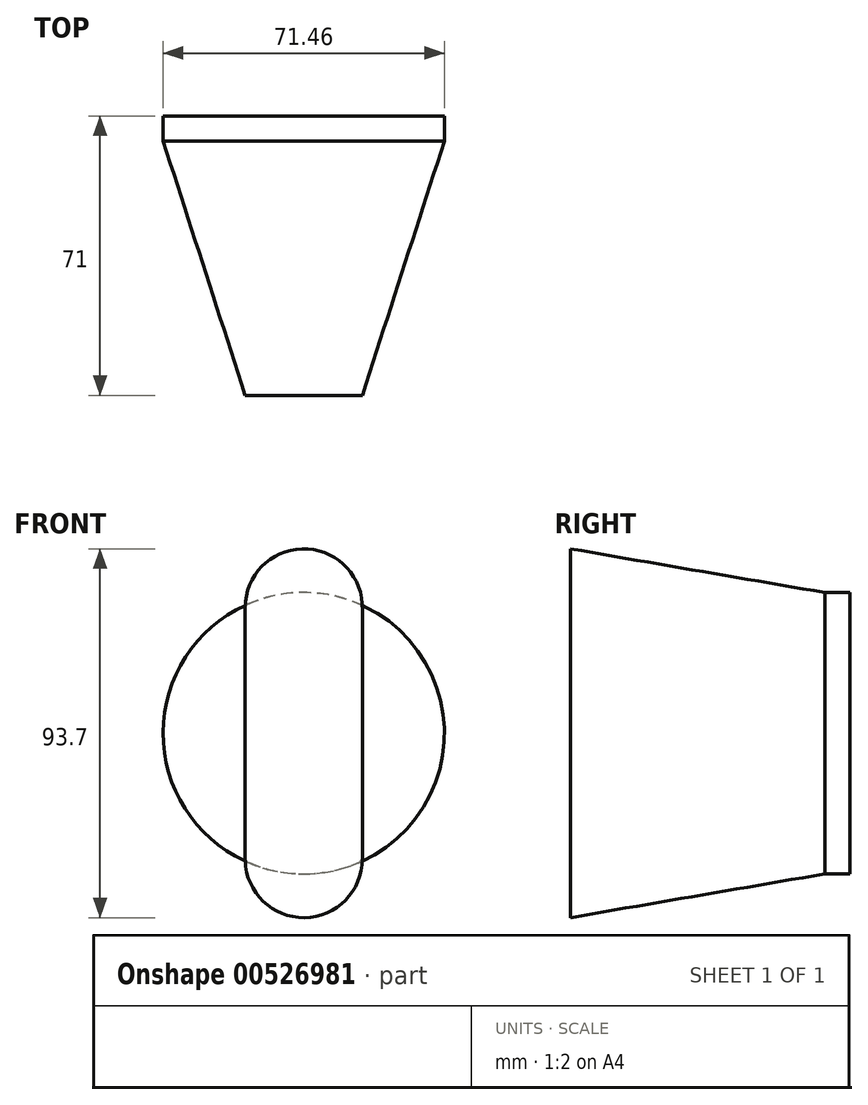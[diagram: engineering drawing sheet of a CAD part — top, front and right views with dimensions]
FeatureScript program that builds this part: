
annotation { "Feature Type Name" : "Feature", "Feature Type Description" : "" }
export const myFeature = defineFeature(function(context is Context, id is Id, definition is map)
    precondition{}
    {
        {
            var Q0;
            Q0=qCreatedBy(makeId("Front.planeOp"),FACE);
            var sketch = newSketch(context, id + "F0", { "sketchPlane" : qUnion([Q0])});
            skCircle(sketch, "E0", {"center": v(0, 0) * mm, "radius": 35.73 * mm});
            skSolve(sketch);
        }
        {
            var Q0;
            Q0=qCreatedBy(makeId("Front.planeOp"),FACE);
            cPlane(context, id + "F1", {"entities" : qUnion([Q0]), "cplaneType" : CPlaneType.OFFSET, "offset" : 67.82 * mm, "width" : 152.4 * mm, "height" : 152.4 * mm});
        }
        {
            var Q0;
            Q0=qCreatedBy(id+"F1.planeOp",FACE);
            var sketch = newSketch(context, id + "F2", { "sketchPlane" : qUnion([Q0])});
            skLineSegment(sketch, "E1.bottom", {"start": v(14.86, -32) * mm, "end": v(-14.86, -32) * mm, "construction": true});
            skLineSegment(sketch, "E1.top", {"start": v(14.86, 32) * mm, "end": v(-14.86, 32) * mm, "construction": true});
            skLineSegment(sketch, "E1.left", {"start": v(14.86, -32) * mm, "end": v(14.86, 32) * mm});
            skLineSegment(sketch, "E1.right", {"start": v(-14.86, -32) * mm, "end": v(-14.86, 32) * mm});
            skPoint(sketch, "E1.middle", {"position": v(0, 0) * mm});
            skArc(sketch, "E2", {"start": v(14.86, 32) * mm, "mid": v(0, 46.85) * mm, "end": v(-14.86, 32) * mm});
            skArc(sketch, "E3", {"start": v(-14.86, -32) * mm, "mid": v(0, -46.85) * mm, "end": v(14.86, -32) * mm});
            skSolve(sketch);
        }
        {
            var Q0;
            Q0=makeQuery(id+"F0.imprint","IMPRINT",FACE,{"disambiguationData":[TD([[makeQuery(id+"F0.imprint","IMPRINT",EDGE,{"derivedFrom":sQuery(id+"F0.wireOp",EDGE,"E0")}),1.0]])]});
            extrude(context, id + "F3", {"entities" : qUnion([Q0]), "endBound" : BoundingType.SYMMETRIC, "depth" : 6.35 * mm, "offsetDistance" : 25.4 * mm});
        }
        {
            var Q0;
            Q0=makeQuery(id+"F3.opExtrude","CAP_FACE",FACE,{"disambiguationData":[OSD([sQuery(id+"F0.wireOp",EDGE,"E0")])],"isStart":false});
            var sketch = newSketch(context, id + "F4", { "sketchPlane" : qUnion([Q0])});
            skArc(sketch, "E4", {"start": v(-14.65, 32.6) * mm, "mid": v(-35.73, 0.27) * mm, "end": v(-15.14, -32.37) * mm});
            skArc(sketch, "E5", {"start": v(15.62, 32.14) * mm, "mid": v(0.53, 35.73) * mm, "end": v(-14.65, 32.6) * mm});
            skArc(sketch, "E6", {"start": v(14.18, -32.8) * mm, "mid": v(35.72, -0.8) * mm, "end": v(15.62, 32.14) * mm});
            skArc(sketch, "E7", {"start": v(-15.14, -32.37) * mm, "mid": v(-0.53, -35.73) * mm, "end": v(14.18, -32.8) * mm});
            skSolve(sketch);
        }
        {
            var Q1;
            Q1=makeQuery(id+"F4.imprint","IMPRINT",FACE,{"disambiguationData":[TD([[makeQuery(id+"F4.imprint","IMPRINT",EDGE,{"derivedFrom":sQuery(id+"F4.wireOp",EDGE,"E4")}),1.0]])]});
            var Q2;
            Q2=makeQuery(id+"F2.imprint","IMPRINT",FACE,{"disambiguationData":[TD([[makeQuery(id+"F2.imprint","IMPRINT",EDGE,{"derivedFrom":sQuery(id+"F2.wireOp",EDGE,"E1.left")}),1.0]])]});
            loft(context, id + "F5", {"operationType" : NewBodyOperationType.ADD, "sheetProfilesArray" : [{ "sheetProfileEntities" : qUnion([Q1]) }, { "sheetProfileEntities" : qUnion([Q2]) }]});
        }
    });
